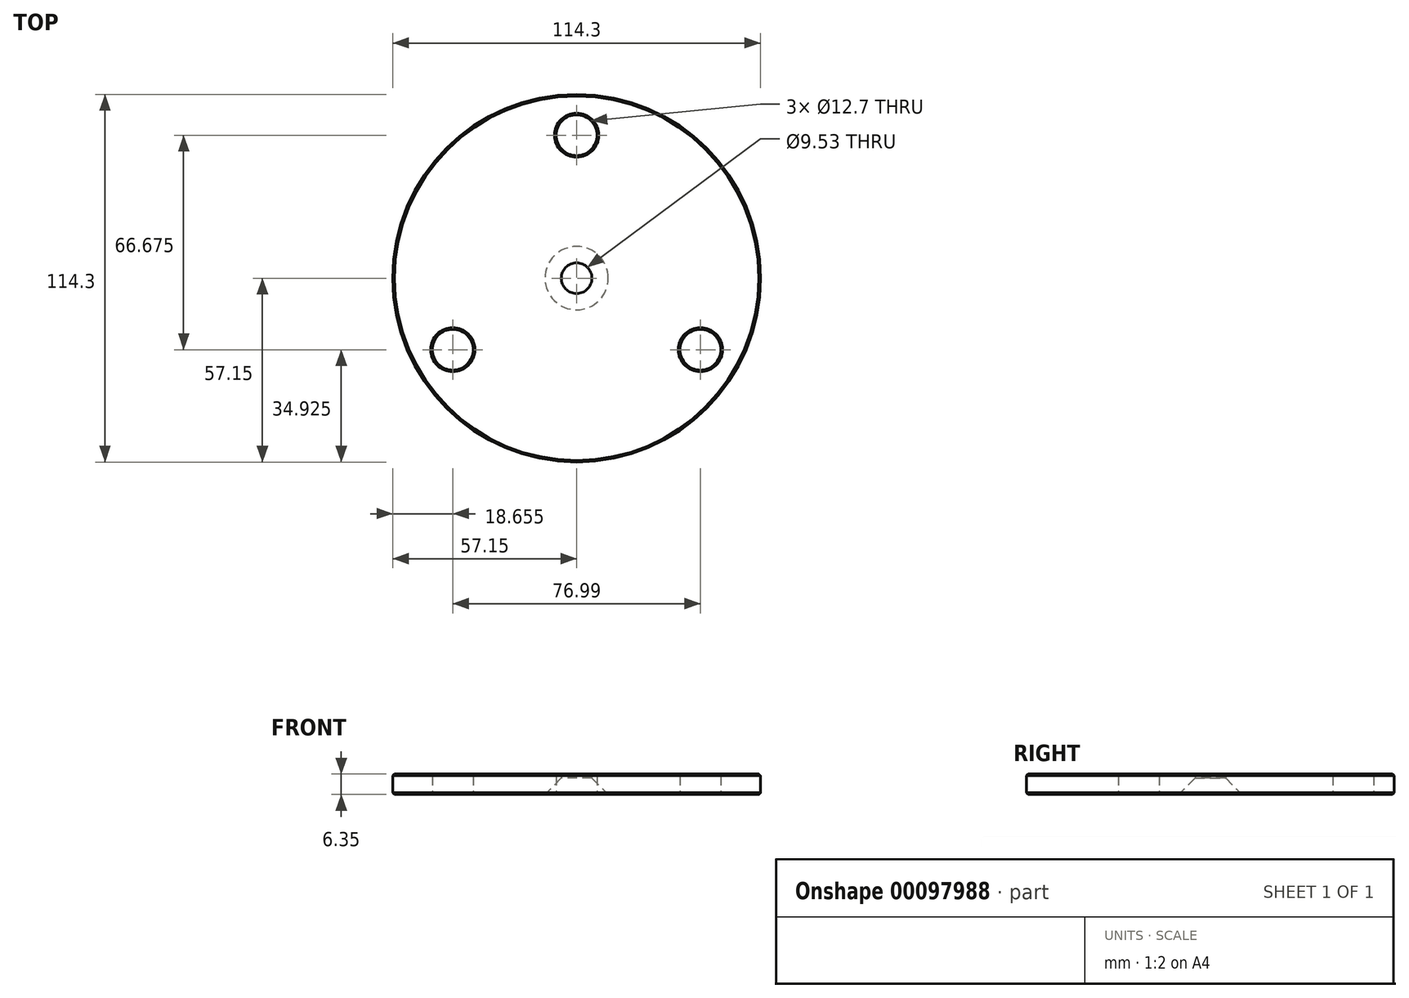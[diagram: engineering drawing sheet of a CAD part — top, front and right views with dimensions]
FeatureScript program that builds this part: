
annotation { "Feature Type Name" : "Feature", "Feature Type Description" : "" }
export const myFeature = defineFeature(function(context is Context, id is Id, definition is map)
    precondition{}
    {
        {
            var Q0;
            Q0=qCreatedBy(makeId("Top.planeOp"),FACE);
            var sketch = newSketch(context, id + "F0", { "sketchPlane" : qUnion([Q0])});
            skPoint(sketch, "E0.middle", {"position": v(0, 0) * mm});
            skLineSegment(sketch, "E1", {"start": v(0, 0) * mm, "end": v(0, 65.78) * mm, "construction": true});
            skLineSegment(sketch, "E2", {"start": v(0, 0) * mm, "end": v(-61, -35.21) * mm, "construction": true});
            skLineSegment(sketch, "E3", {"start": v(0, 0) * mm, "end": v(67.12, -38.75) * mm, "construction": true});
            skCircle(sketch, "E4", {"center": v(0, 0) * mm, "radius": 44.45 * mm, "construction": true});
            skCircle(sketch, "E5", {"center": v(0, 44.45) * mm, "radius": 6.35 * mm});
            skPoint(sketch, "E5.centerSnap0", {"position": v(0, 32.9) * mm});
            skCircle(sketch, "E6", {"center": v(38.5, -22.22) * mm, "radius": 6.35 * mm});
            skCircle(sketch, "E7", {"center": v(-38.5, -22.22) * mm, "radius": 6.35 * mm});
            skCircle(sketch, "E8", {"center": v(0, 0) * mm, "radius": 57.15 * mm});
            skCircle(sketch, "E9", {"center": v(0, 0) * mm, "radius": 4.76 * mm});
            skSolve(sketch);
        }
        {
            var Q0;
            Q0=makeQuery(id+"F0.imprint","IMPRINT",FACE,{"disambiguationData":[TD([[makeQuery(id+"F0.imprint","IMPRINT",EDGE,{"derivedFrom":sQuery(id+"F0.wireOp",EDGE,"E0.bottom")}),-1.0]])]});
            var Q1;
            Q1=makeQuery(id+"F0.imprint","IMPRINT",FACE,{"disambiguationData":[TD([[makeQuery(id+"F0.imprint","IMPRINT",EDGE,{"derivedFrom":sQuery(id+"F0.wireOp",EDGE,"E5")}),-1.0]])]});
            extrude(context, id + "F1", {"entities" : qUnion([Q0, Q1]), "depth" : 6.35 * mm});
        }
        {
            var Q0;
            Q0=makeQuery(id+"F1.opExtrude","CAP_EDGE",EDGE,{"disambiguationData":[OSD([sQuery(id+"F0.wireOp",EDGE,"E8")])],"isStart":false});
            var Q1;
            Q1=makeQuery(id+"F1.opExtrude","CAP_EDGE",EDGE,{"disambiguationData":[OSD([sQuery(id+"F0.wireOp",EDGE,"E5")])],"isStart":false});
            var Q2;
            Q2=makeQuery(id+"F1.opExtrude","CAP_EDGE",EDGE,{"disambiguationData":[OSD([sQuery(id+"F0.wireOp",EDGE,"E7")])],"isStart":false});
            var Q3;
            Q3=makeQuery(id+"F1.opExtrude","CAP_EDGE",EDGE,{"disambiguationData":[OSD([sQuery(id+"F0.wireOp",EDGE,"E6")])],"isStart":false});
            var Q4;
            Q4=makeQuery(id+"F1.opExtrude","CAP_EDGE",EDGE,{"disambiguationData":[OSD([sQuery(id+"F0.wireOp",EDGE,"E8")])],"isStart":true});
            var Q5;
            Q5=makeQuery(id+"F1.opExtrude","CAP_EDGE",EDGE,{"disambiguationData":[OSD([sQuery(id+"F0.wireOp",EDGE,"E5")])],"isStart":true});
            var Q6;
            Q6=makeQuery(id+"F1.opExtrude","CAP_EDGE",EDGE,{"disambiguationData":[OSD([sQuery(id+"F0.wireOp",EDGE,"E6")])],"isStart":true});
            var Q7;
            Q7=makeQuery(id+"F1.opExtrude","CAP_EDGE",EDGE,{"disambiguationData":[OSD([sQuery(id+"F0.wireOp",EDGE,"E7")])],"isStart":true});
            chamfer(context, id + "F2", {"entities" : qUnion([Q0, Q1, Q2, Q3, Q4, Q5, Q6, Q7]), "width" : 0.5 * mm, "tangentPropagation" : true});
        }
        {
            var Q0;
            Q0=makeQuery(id+"F1.opExtrude","CAP_EDGE",EDGE,{"disambiguationData":[OSD([sQuery(id+"F0.wireOp",EDGE,"E9")])],"isStart":true});
            chamfer(context, id + "F3", {"entities" : qUnion([Q0]), "width" : 5.08 * mm, "tangentPropagation" : true});
        }
    });
